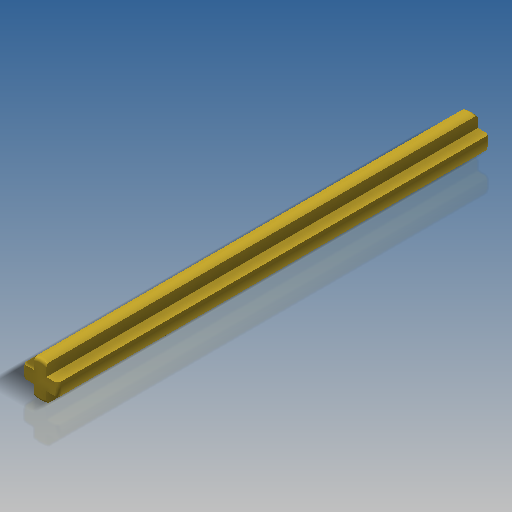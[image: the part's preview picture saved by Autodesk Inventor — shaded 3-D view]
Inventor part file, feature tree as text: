
AUTODESK INVENTOR PART (.ipt)
format: ipt  version: 2019.4 (Build 234330000, 330)  size: 177,664 bytes
history: native  units: in
note: dims shown in document units (in); Inventor stores cm internally (conversion verified against a paired STEP export)
features: extrude x1, fillet x1, sketch x1
ambient origin geometry x8: Origin, YZ Plane, XZ Plane, XY Plane, X Axis, Y Axis, Z Axis, Center Point
bodies: Solid1 (feature_tree)
feature tree (3):
  extrude  "Extrusion1"  Depth=0.0157in
  fillet  "Fillet1"  Radius=2.2047in
  sketch  "Sketch1"  dims[d0=0.189in d1=0.063in d2=2.2047in d3=0.0in d4=0.0157in d5=0.0in d6=0.0in]
